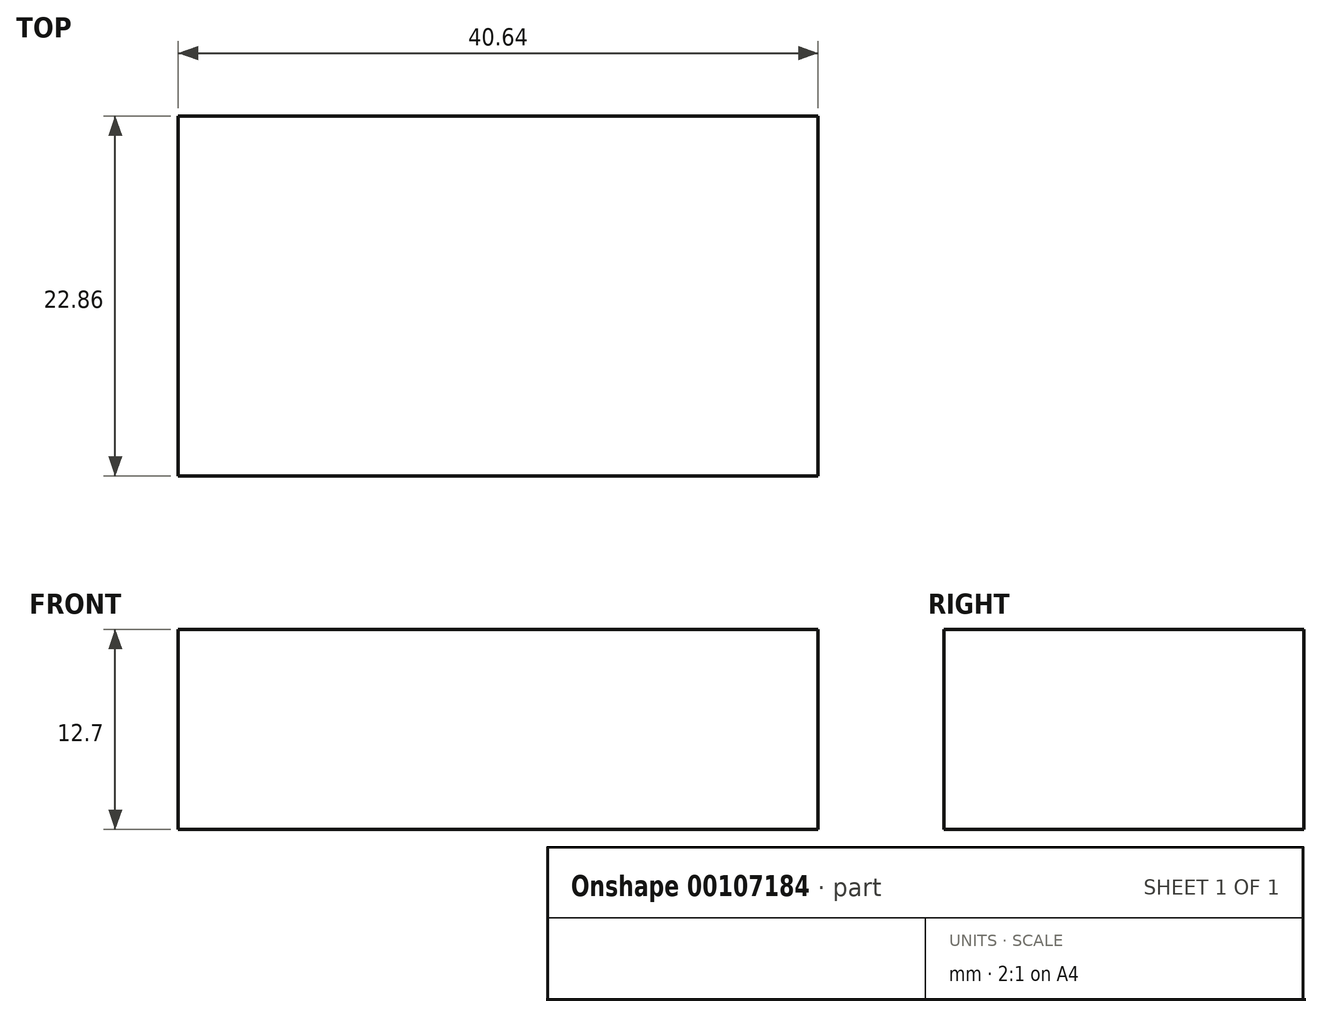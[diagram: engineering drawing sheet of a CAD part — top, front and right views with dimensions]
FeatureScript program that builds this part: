
annotation { "Feature Type Name" : "Feature", "Feature Type Description" : "" }
export const myFeature = defineFeature(function(context is Context, id is Id, definition is map)
    precondition{}
    {
        {
            var Q0;
            Q0=qCreatedBy(makeId("Top.planeOp"),FACE);
            var sketch = newSketch(context, id + "F0", { "sketchPlane" : qUnion([Q0])});
            skLineSegment(sketch, "E0.bottom", {"start": v(-20.32, 11.43) * mm, "end": v(20.32, 11.43) * mm});
            skLineSegment(sketch, "E0.top", {"start": v(-20.32, -11.43) * mm, "end": v(20.32, -11.43) * mm});
            skLineSegment(sketch, "E0.left", {"start": v(-20.32, 11.43) * mm, "end": v(-20.32, -11.43) * mm});
            skLineSegment(sketch, "E0.right", {"start": v(20.32, 11.43) * mm, "end": v(20.32, -11.43) * mm});
            skPoint(sketch, "E0.middle", {"position": v(0, 0) * mm});
            skSolve(sketch);
        }
        {
            var Q0;
            Q0=makeQuery(id+"F0.imprint","IMPRINT",FACE,{"disambiguationData":[TD([[makeQuery(id+"F0.imprint","IMPRINT",EDGE,{"derivedFrom":sQuery(id+"F0.wireOp",EDGE,"E0.bottom")}),-1.0]])]});
            extrude(context, id + "F1", {"entities" : qUnion([Q0]), "depth" : 12.7 * mm});
        }
    });
